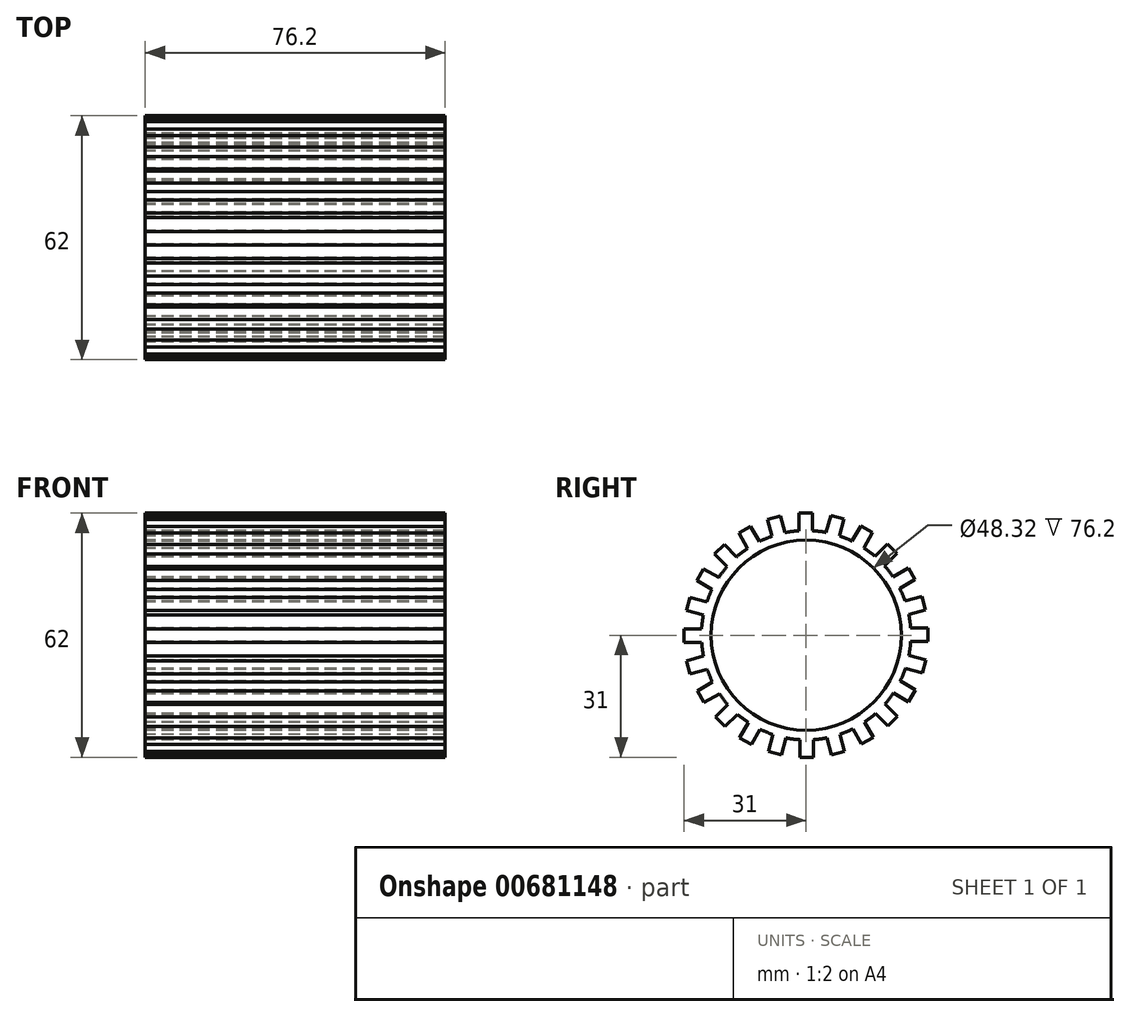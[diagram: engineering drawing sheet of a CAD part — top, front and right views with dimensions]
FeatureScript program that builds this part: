
annotation { "Feature Type Name" : "Feature", "Feature Type Description" : "" }
export const myFeature = defineFeature(function(context is Context, id is Id, definition is map)
    precondition{}
    {
        {
            var Q0;
            Q0=qCreatedBy(makeId("Right.planeOp"),FACE);
            var sketch = newSketch(context, id + "F0", { "sketchPlane" : qUnion([Q0])});
            skCircle(sketch, "E0", {"center": v(0, 0) * mm, "radius": 26.6 * mm});
            skLineSegment(sketch, "E1", {"start": v(-1.84, 26.54) * mm, "end": v(-1.84, 31) * mm});
            skLineSegment(sketch, "E2", {"start": v(-1.84, 31) * mm, "end": v(1.6, 31) * mm});
            skLineSegment(sketch, "E3", {"start": v(1.6, 31) * mm, "end": v(1.6, 26.55) * mm});
            skLineSegment(sketch, "E4", {"start": v(0, 0) * mm, "end": v(0, 26.55) * mm, "construction": true});
            skCircle(sketch, "E5", {"center": v(0, 0) * mm, "radius": 24.16 * mm});
            skSolve(sketch);
        }
        {
            var Q0;
            Q0 = qSketchRegion(id + "F0", true);
            extrude(context, id + "F1", {"entities" : qUnion([Q0]), "endBound" : BoundingType.SYMMETRIC, "depth" : 76.2 * mm, "offsetDistance" : 25.4 * mm});
        }
        {
            var Q0;
            Q0=makeQuery(id+"F1.opExtrude","SWEPT_BODY",BODY,{"disambiguationData":[OSD([sQuery(id+"F0.wireOp",EDGE,"E0"),sQuery(id+"F0.wireOp",EDGE,"E1"),sQuery(id+"F0.wireOp",EDGE,"E2"),sQuery(id+"F0.wireOp",EDGE,"E3"),sQuery(id+"F0.wireOp",EDGE,"e0007d45-513e-46c6-bb31-e5d0ca607b860.MirrorCS"),sQuery(id+"F0.wireOp",EDGE,"e0007d45-513e-46c6-bb31-e5d0ca607b861.MirrorCS"),sQuery(id+"F0.wireOp",EDGE,"e0007d45-513e-46c6-bb31-e5d0ca607b862.MirrorCS")])]});
            var Q1;
            {var subQ0=sQuery(id+"F0.wireOp",EDGE,"E0");Q1=makeQuery(id+"F1.opExtrude","SWEPT_FACE",FACE,{"disambiguationData":[OSD([subQ0]),TDD([makeQuery(id+"F0.imprint","IMPRINT",EDGE,{"disambiguationData":[TD([[makeQuery(id+"F0.imprint","INTERSECT",VERTEX,{"derivedFrom":[subQ0,sQuery(id+"F0.wireOp",EDGE,"E3")]}),1.0]])],"derivedFrom":subQ0})])]});}
            circularPattern(context, id + "F2", {"operationType" : NewBodyOperationType.ADD, "entities" : qUnion([Q0]), "axis" : qUnion([Q1]), "angle" : 360 * degree, "instanceCount" : 24, "equalSpace" : true});
        }
    });
